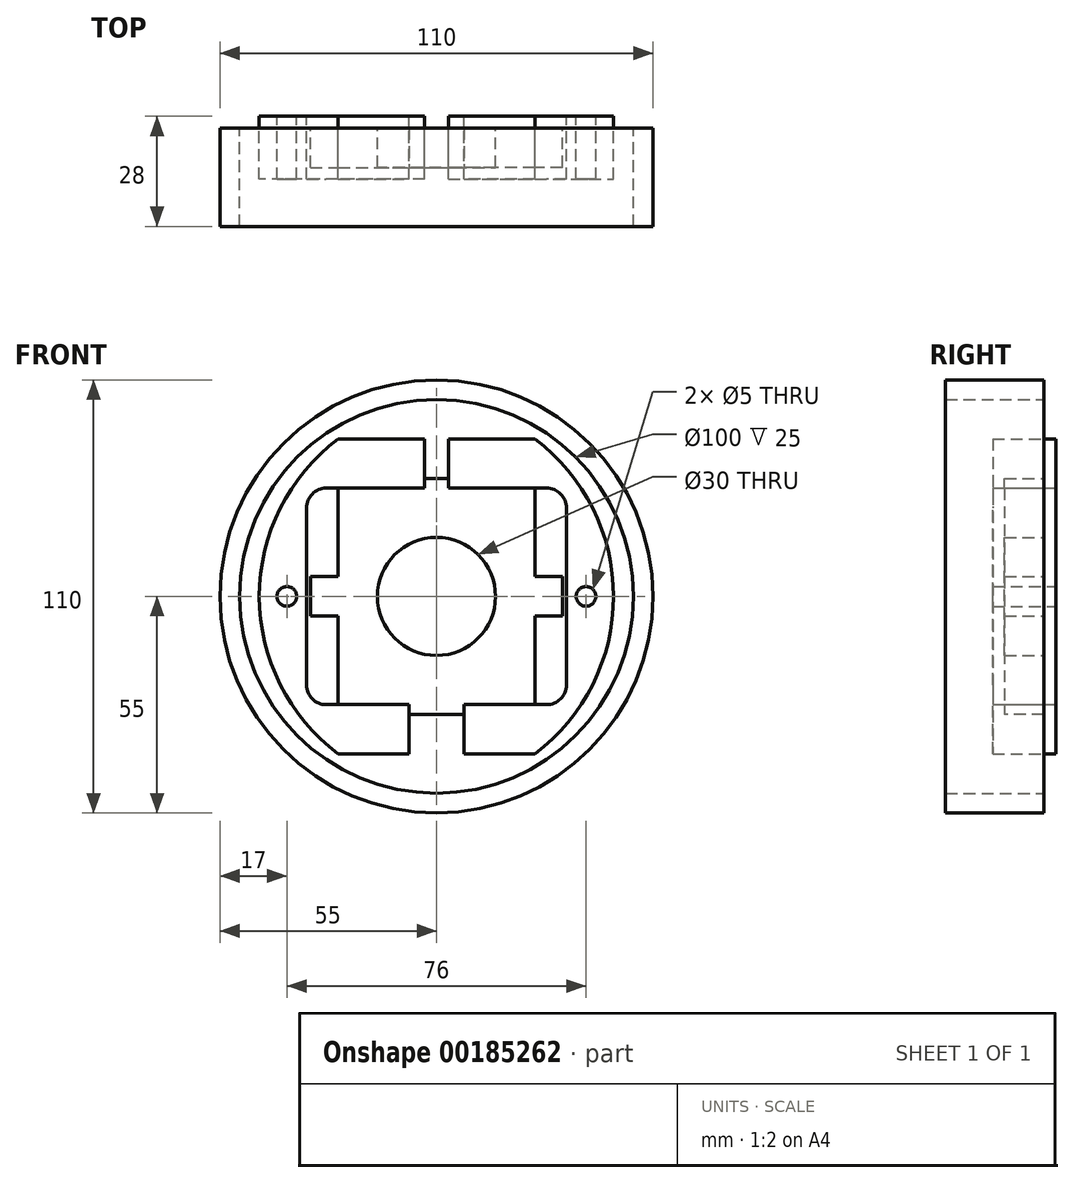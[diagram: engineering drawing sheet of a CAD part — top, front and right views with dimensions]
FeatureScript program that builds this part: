
annotation { "Feature Type Name" : "Feature", "Feature Type Description" : "" }
export const myFeature = defineFeature(function(context is Context, id is Id, definition is map)
    precondition{}
    {
        {
            var Q0;
            Q0=qCreatedBy(makeId("Front.planeOp"),FACE);
            var sketch = newSketch(context, id + "F0", { "sketchPlane" : qUnion([Q0])});
            skCircle(sketch, "E0", {"center": v(0, 0) * mm, "radius": 15 * mm});
            skLineSegment(sketch, "E1.bottom", {"start": v(-25, 30) * mm, "end": v(25, 30) * mm});
            skLineSegment(sketch, "E1.top", {"start": v(-25, -30) * mm, "end": v(25, -30) * mm});
            skLineSegment(sketch, "E1.left", {"start": v(-25, 30) * mm, "end": v(-25, -30) * mm});
            skLineSegment(sketch, "E1.right", {"start": v(25, 30) * mm, "end": v(25, -30) * mm});
            skSolve(sketch);
        }
        {
            var Q0;
            Q0 = qSketchRegion(id + "F0", true);
            extrude(context, id + "F1", {"entities" : qUnion([Q0]), "depth" : 10 * mm});
        }
        {
            var Q0;
            Q0=qCreatedBy(makeId("Front.planeOp"),FACE);
            var sketch = newSketch(context, id + "F2", { "sketchPlane" : qUnion([Q0])});
            skArc(sketch, "E2", {"start": v(-25, 40) * mm, "mid": v(-45, 0) * mm, "end": v(-25, -40) * mm});
            skLineSegment(sketch, "E3", {"start": v(-3, 40) * mm, "end": v(-25, 40) * mm});
            skLineSegment(sketch, "E4", {"start": v(-25, -40) * mm, "end": v(-6.95, -40) * mm});
            skLineSegment(sketch, "E5", {"start": v(-3, 40) * mm, "end": v(-3, 27.5) * mm});
            skLineSegment(sketch, "E6", {"start": v(-3, 27.5) * mm, "end": v(-28, 27.5) * mm});
            skLineSegment(sketch, "E7", {"start": v(-6.95, -40) * mm, "end": v(-6.95, -27.5) * mm});
            skLineSegment(sketch, "E8", {"start": v(-6.95, -27.5) * mm, "end": v(-28, -27.5) * mm});
            skLineSegment(sketch, "E9", {"start": v(-33, -22.5) * mm, "end": v(-33, 22.5) * mm});
            skPoint(sketch, "E10.visualSharp", {"position": v(-33, 27.5) * mm});
            skArc(sketch, "E10.filletArc", {"start": v(-28, 27.5) * mm, "mid": v(-31.54, 26.04) * mm, "end": v(-33, 22.5) * mm});
            skPoint(sketch, "E11.visualSharp", {"position": v(-33, -27.5) * mm});
            skArc(sketch, "E11.filletArc", {"start": v(-33, -22.5) * mm, "mid": v(-31.54, -26.04) * mm, "end": v(-28, -27.5) * mm});
            skCircle(sketch, "E12", {"center": v(-38, 0) * mm, "radius": 2.5 * mm});
            skSolve(sketch);
        }
        {
            var Q0;
            Q0=makeQuery(id+"F2.imprint","IMPRINT",FACE,{"disambiguationData":[TD([[makeQuery(id+"F2.imprint","IMPRINT",EDGE,{"derivedFrom":sQuery(id+"F2.wireOp",EDGE,"E2")}),1.0]])]});
            extrude(context, id + "F3", {"entities" : qUnion([Q0]), "operationType" : NewBodyOperationType.ADD, "depth" : 13 * mm, "hasSecondDirection" : true, "secondDirectionOppositeDirection" : true, "secondDirectionDepth" : 3 * mm});
        }
        {
            var Q0;
            Q0=makeQuery(id+"F1.opExtrude","SWEPT_FACE",FACE,{"disambiguationData":[OSD([sQuery(id+"F0.wireOp",EDGE,"E1.left")])]});
            var sketch = newSketch(context, id + "F4", { "sketchPlane" : qUnion([Q0])});
            skLineSegment(sketch, "E13.bottom", {"start": v(10, -5) * mm, "end": v(0, -5) * mm});
            skLineSegment(sketch, "E13.top", {"start": v(10, 5) * mm, "end": v(0, 5) * mm});
            skLineSegment(sketch, "E13.left", {"start": v(10, -5) * mm, "end": v(10, 5) * mm});
            skLineSegment(sketch, "E13.right", {"start": v(0, -5) * mm, "end": v(0, 5) * mm});
            skPoint(sketch, "E13.middle", {"position": v(5, 0) * mm});
            skSolve(sketch);
        }
        {
            var Q0;
            Q0 = qSketchRegion(id + "F4", true);
            extrude(context, id + "F5", {"entities" : qUnion([Q0]), "operationType" : NewBodyOperationType.ADD, "depth" : 7 * mm});
        }
        {
            var Q0;
            Q0=makeQuery(id+"F1.opExtrude","SWEPT_BODY",BODY,{"disambiguationData":[OSD([sQuery(id+"F0.wireOp",EDGE,"E0"),sQuery(id+"F0.wireOp",EDGE,"E1.bottom"),sQuery(id+"F0.wireOp",EDGE,"E1.top"),sQuery(id+"F0.wireOp",EDGE,"E1.left"),sQuery(id+"F0.wireOp",EDGE,"E1.right")])]});
            var Q1;
            Q1=qCreatedBy(makeId("Right.planeOp"),FACE);
            mirror(context, id + "F6", {"operationType" : NewBodyOperationType.ADD, "entities" : qUnion([Q0]), "mirrorPlane" : qUnion([Q1])});
        }
        {
            var Q0;
            Q0=qCreatedBy(makeId("Front.planeOp"),FACE);
            var sketch = newSketch(context, id + "F7", { "sketchPlane" : qUnion([Q0])});
            skCircle(sketch, "E14", {"center": v(0, 0) * mm, "radius": 55 * mm});
            skCircle(sketch, "E15", {"center": v(0, 0) * mm, "radius": 50 * mm});
            skSolve(sketch);
        }
        {
            var Q0;
            Q0 = qSketchRegion(id + "F7", true);
            var Q1;
            Q1=makeQuery(id+"F0y70HJvtDZf4l0_1.imprint","IMPRINT",FACE,{"disambiguationData":[TD([[makeQuery(id+"F0y70HJvtDZf4l0_1.imprint","IMPRINT",EDGE,{"derivedFrom":sQuery(id+"F0y70HJvtDZf4l0_1.wireOp",EDGE,"mQhdz8Jz-rnw4-TFed-hHZH-VmEtTxFpvONa")}),-1.0]])]});
            extrude(context, id + "F8", {"entities" : qUnion([Q0, Q1]), "depth" : 25 * mm});
        }
    });
